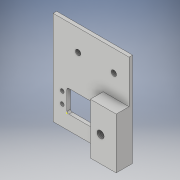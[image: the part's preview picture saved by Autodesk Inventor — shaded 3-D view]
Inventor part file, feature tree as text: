
AUTODESK INVENTOR PART (.ipt)
format: ipt  version: 2017 (Build 210142000, 142)  size: 266,752 bytes
history: native  units: in
note: dims shown in document units (in); Inventor stores cm internally (conversion verified against a paired STEP export)
features: sketch x14, extrude x12, thread x7, fillet x4, projected_geometry x3, hole x1
ambient origin geometry x8: Origin, YZ Plane, XZ Plane, XY Plane, X Axis, Y Axis, Z Axis, Center Point
bodies: Solid1 (feature_tree)
feature tree (41):
  extrude  "Extrusion1"  Depth=0.78in
  extrude  "Extrusion2"  Depth=0.125in
  extrude  "Extrusion3"  Depth=0.125in
  extrude  "Extrusion4"  Depth=0.135in
  extrude  "Extrusion7"  Depth=0.125in TaperAngle=0.0deg
  sketch  "Sketch9"  dims[d21=0.125in d22=0.324in d23=0.0in d33=0.75in d34=0.324in d35=0.0in d36=1.78in d41=0.25in]
  extrude  "Extrusion9"  Depth=0.324in TaperAngle=0.0deg
  thread  "Thread1"  [1 undecoded]
  thread  "Thread2"  [1 undecoded]
  thread  "Thread3"  [1 undecoded]
  thread  "Thread4"  [1 undecoded]
  extrude  "Extrusion10"  Depth=0.2in
  hole  "Hole1"  [1 undecoded]
  extrude  "Extrusion11"  Depth=1.0in TaperAngle=0.0deg
  sketch  "Sketch14"  dims[d58=0.356in d59=0.25in]
  extrude  "Extrusion12"  Depth=0.125in TaperAngle=0.0deg
  extrude  "Extrusion15"  Depth=0.25in
  thread  "Thread5"  [1 undecoded]
  thread  "Thread6"  [1 undecoded]
  sketch  "Sketch18"  dims[d74=0.45in d75=0.45in d82=0.19in d83=0.19in d84=1.0in d85=0.0in d86=1.0in d87=0.0in d88=1.0in d89=0.0in d90=0.38in d91=0.25in d92=0.0in d93=1.0in d94=0.0in d95=1.78in d96=2.528in d98=0.5in d99=0.25in d100=0.0in d101=0.06in d102=0.06in d103=0.06in d104=0.06in d106=0.484in d107=0.165in d108=1.56in d109=0.693in d110=1.087in d111=0.165in d112=0.165in d113=0.165in]
  extrude  "Extrusion16"  Depth=0.874in
  thread  "Thread7"  [1 undecoded]
  extrude  "Extrusion17"  Depth=1.56in
  fillet  "Fillet1"  Radius=0.19in
  fillet  "Fillet2"  Radius=0.19in
  fillet  "Fillet3"  Radius=1.0in
  fillet  "Fillet4"  Radius=1.0in
  sketch  "Sketch1"  dims[d0=1.56in d1=0.78in]
  sketch  "Sketch2"  dims[d6=0.125in d7=0.0in d10=0.083in]
  sketch  "Sketch3"  dims[d11=0.125in d12=0.0in d15=0.135in]
  sketch  "Sketch4"  dims[d16=0.135in d17=0.135in]
  sketch  "Sketch8"  dims[d18=0.135in d19=0.125in d20=0.0in]
  sketch  "Sketch10"  dims[d44=0.2in d45=0.0in d46=1.89in]
  sketch  "Sketch11"  dims[d47=1.89in d48=1.0in d49=0.0in]
  sketch  "Sketch12"  dims[d50=1.0in d51=0.0in d52=1.0in d53=0.0in]
  projected_geometry  "Projected Loop1"
  projected_geometry  "Projected Loop2"
  projected_geometry  "Projected Loop3"
  sketch  "Sketch13"  dims[d54=1.0in d55=0.0in d56=0.125in d57=0.0in]
  sketch  "Sketch15"  dims[d60=0.25in d61=0.75in d62=0.375in d63=0.25in d64=0.5635in d65=0.25in d66=0.0in d67=0.01in d68=0.0in d69=1.5in d70=0.0in]
  sketch  "Sketch16"  dims[d71=0.75in d72=0.874in d73=0.53in]
note: 8 required parameter values undecoded (feature->parameter linkage not recoverable at this tier; creation-order binding heuristic only, values carry confidence <= 0.55)
